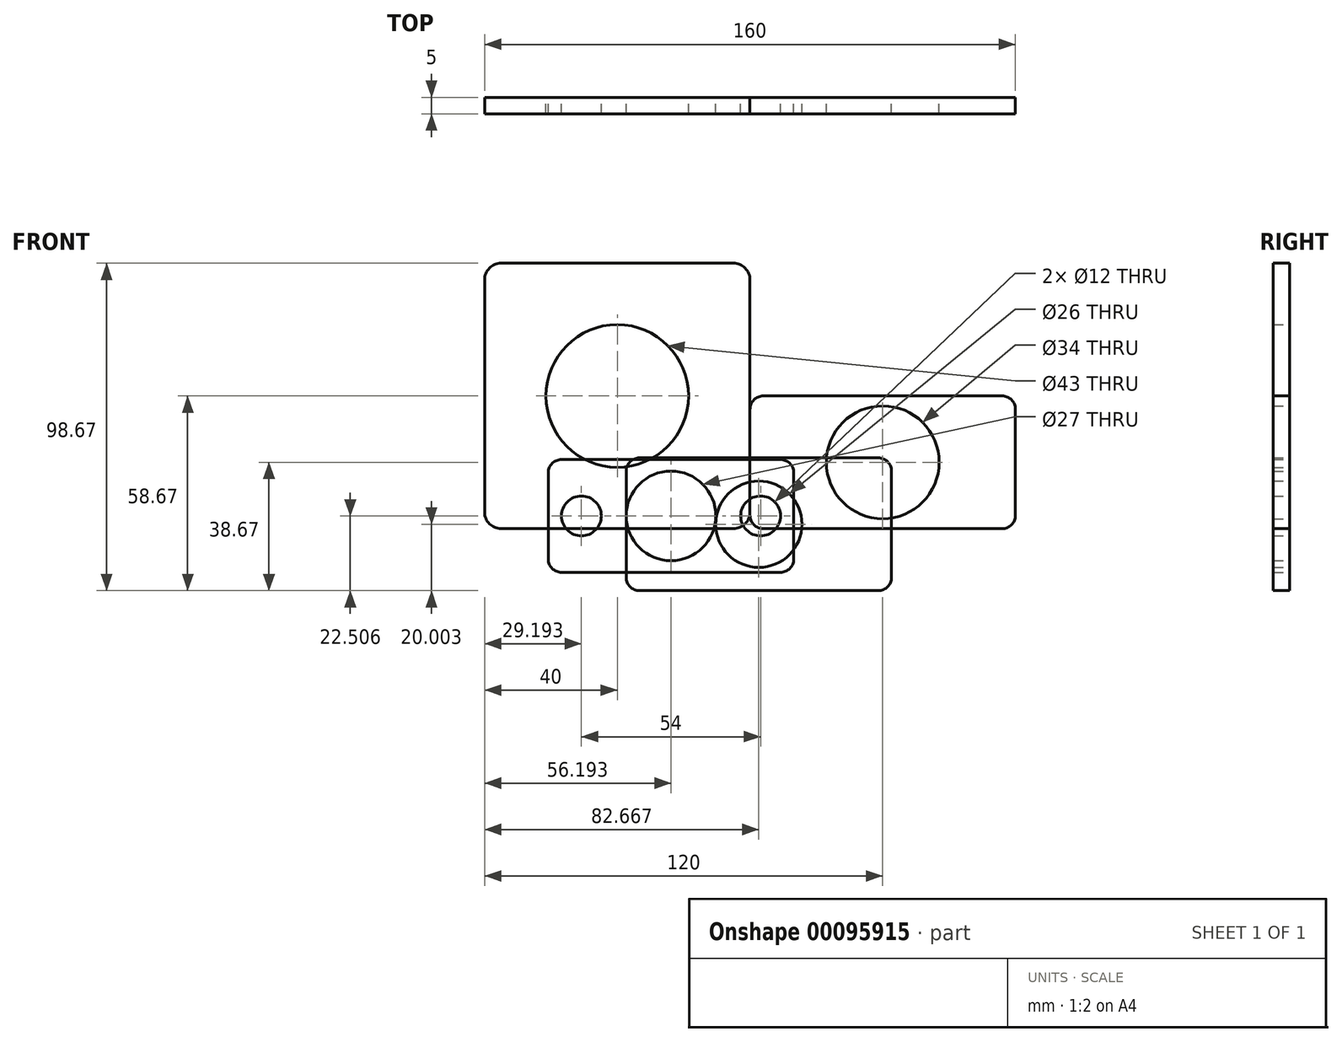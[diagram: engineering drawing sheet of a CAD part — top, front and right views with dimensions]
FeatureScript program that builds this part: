
annotation { "Feature Type Name" : "Feature", "Feature Type Description" : "" }
export const myFeature = defineFeature(function(context is Context, id is Id, definition is map)
    precondition{}
    {
        {
            var Q0;
            Q0=qCreatedBy(makeId("Front.planeOp"),FACE);
            var sketch = newSketch(context, id + "F0", { "sketchPlane" : qUnion([Q0])});
            skLineSegment(sketch, "E0.bottom", {"start": v(4, 0) * mm, "end": v(76, 0) * mm});
            skLineSegment(sketch, "E0.top", {"start": v(4, 40) * mm, "end": v(76, 40) * mm});
            skLineSegment(sketch, "E0.left", {"start": v(0, 4) * mm, "end": v(0, 36) * mm});
            skLineSegment(sketch, "E0.right", {"start": v(80, 4) * mm, "end": v(80, 36) * mm});
            skPoint(sketch, "E1.visualSharp", {"position": v(0, 40) * mm});
            skArc(sketch, "E1.filletArc", {"start": v(4, 40) * mm, "mid": v(1.17, 38.83) * mm, "end": v(0, 36) * mm});
            skPoint(sketch, "E2.visualSharp", {"position": v(80, 40) * mm});
            skArc(sketch, "E2.filletArc", {"start": v(80, 36) * mm, "mid": v(78.83, 38.83) * mm, "end": v(76, 40) * mm});
            skPoint(sketch, "E3.visualSharp", {"position": v(80, 0) * mm});
            skArc(sketch, "E3.filletArc", {"start": v(76, 0) * mm, "mid": v(78.83, 1.17) * mm, "end": v(80, 4) * mm});
            skPoint(sketch, "E4.visualSharp", {"position": v(0, 0) * mm});
            skArc(sketch, "E4.filletArc", {"start": v(0, 4) * mm, "mid": v(1.17, 1.17) * mm, "end": v(4, 0) * mm});
            skSolve(sketch);
        }
        {
            var Q0;
            Q0=makeQuery(id+"F0.imprint","IMPRINT",FACE,{"disambiguationData":[TD([[makeQuery(id+"F0.imprint","IMPRINT",EDGE,{"derivedFrom":sQuery(id+"F0.wireOp",EDGE,"E0.bottom")}),1.0]])]});
            extrude(context, id + "F1", {"entities" : qUnion([Q0]), "depth" : 5 * mm, "offsetDistance" : 25 * mm});
        }
        {
            var Q0;
            Q0=qCreatedBy(makeId("Front.planeOp"),FACE);
            var sketch = newSketch(context, id + "F2", { "sketchPlane" : qUnion([Q0])});
            skLineSegment(sketch, "E5.bottom", {"start": v(4, 0) * mm, "end": v(76, 0) * mm});
            skLineSegment(sketch, "E5.top", {"start": v(4, 40) * mm, "end": v(76, 40) * mm});
            skLineSegment(sketch, "E5.left", {"start": v(0, 4) * mm, "end": v(0, 36) * mm});
            skLineSegment(sketch, "E5.right", {"start": v(80, 4) * mm, "end": v(80, 36) * mm});
            skPoint(sketch, "E6.visualSharp", {"position": v(0, 40) * mm});
            skArc(sketch, "E6.filletArc", {"start": v(4, 40) * mm, "mid": v(1.17, 38.83) * mm, "end": v(0, 36) * mm});
            skPoint(sketch, "E7.visualSharp", {"position": v(80, 40) * mm});
            skArc(sketch, "E7.filletArc", {"start": v(80, 36) * mm, "mid": v(78.83, 38.83) * mm, "end": v(76, 40) * mm});
            skPoint(sketch, "E8.visualSharp", {"position": v(80, 0) * mm});
            skArc(sketch, "E8.filletArc", {"start": v(76, 0) * mm, "mid": v(78.83, 1.17) * mm, "end": v(80, 4) * mm});
            skPoint(sketch, "E9.visualSharp", {"position": v(0, 0) * mm});
            skArc(sketch, "E9.filletArc", {"start": v(0, 4) * mm, "mid": v(1.17, 1.17) * mm, "end": v(4, 0) * mm});
            skCircle(sketch, "E10", {"center": v(40, 20) * mm, "radius": 17 * mm});
            skPoint(sketch, "E10.centerSnap0", {"position": v(40, 0) * mm});
            skPoint(sketch, "E10.centerSnap1", {"position": v(0, 20) * mm});
            skSolve(sketch);
        }
        {
            var Q0;
            Q0=makeQuery(id+"F2.imprint","IMPRINT",FACE,{"disambiguationData":[TD([[makeQuery(id+"F2.imprint","IMPRINT",EDGE,{"derivedFrom":sQuery(id+"F2.wireOp",EDGE,"E5.bottom")}),1.0]])]});
            extrude(context, id + "F3", {"entities" : qUnion([Q0]), "depth" : 5 * mm, "offsetDistance" : 25 * mm});
        }
        {
            var Q0;
            Q0=qCreatedBy(makeId("Front.planeOp"),FACE);
            var sketch = newSketch(context, id + "F4", { "sketchPlane" : qUnion([Q0])});
            skLineSegment(sketch, "E11.bottom", {"start": v(-33.33, -18.67) * mm, "end": v(38.67, -18.67) * mm});
            skLineSegment(sketch, "E11.top", {"start": v(-33.33, 21.33) * mm, "end": v(38.67, 21.33) * mm});
            skLineSegment(sketch, "E11.left", {"start": v(-37.33, -14.67) * mm, "end": v(-37.33, 17.33) * mm});
            skLineSegment(sketch, "E11.right", {"start": v(42.67, -14.67) * mm, "end": v(42.67, 17.33) * mm});
            skPoint(sketch, "E12.visualSharp", {"position": v(-37.33, 21.33) * mm});
            skArc(sketch, "E12.filletArc", {"start": v(-33.33, 21.33) * mm, "mid": v(-36.16, 20.16) * mm, "end": v(-37.33, 17.33) * mm});
            skPoint(sketch, "E13.visualSharp", {"position": v(42.67, 21.33) * mm});
            skArc(sketch, "E13.filletArc", {"start": v(42.67, 17.33) * mm, "mid": v(41.5, 20.16) * mm, "end": v(38.67, 21.33) * mm});
            skPoint(sketch, "E14.visualSharp", {"position": v(42.67, -18.67) * mm});
            skArc(sketch, "E14.filletArc", {"start": v(38.67, -18.67) * mm, "mid": v(41.5, -17.5) * mm, "end": v(42.67, -14.67) * mm});
            skPoint(sketch, "E15.visualSharp", {"position": v(-37.33, -18.67) * mm});
            skArc(sketch, "E15.filletArc", {"start": v(-37.33, -14.67) * mm, "mid": v(-36.16, -17.5) * mm, "end": v(-33.33, -18.67) * mm});
            skCircle(sketch, "E16", {"center": v(2.67, 1.33) * mm, "radius": 13 * mm});
            skPoint(sketch, "E16.centerSnap0", {"position": v(2.67, -18.67) * mm});
            skPoint(sketch, "E16.centerSnap1", {"position": v(-37.33, 1.33) * mm});
            skSolve(sketch);
        }
        {
            var Q0;
            Q0 = qSketchRegion(id + "F4", true);
            extrude(context, id + "F5", {"entities" : qUnion([Q0]), "depth" : 5 * mm, "offsetDistance" : 25 * mm});
        }
        {
            var Q0;
            Q0=qCreatedBy(makeId("Front.planeOp"),FACE);
            var sketch = newSketch(context, id + "F6", { "sketchPlane" : qUnion([Q0])});
            skLineSegment(sketch, "E17.bottom", {"start": v(-56.8, -13.16) * mm, "end": v(9.2, -13.16) * mm});
            skLineSegment(sketch, "E17.top", {"start": v(-56.8, 20.84) * mm, "end": v(9.2, 20.84) * mm});
            skLineSegment(sketch, "E17.left", {"start": v(-60.8, -9.16) * mm, "end": v(-60.8, 16.84) * mm});
            skLineSegment(sketch, "E17.right", {"start": v(13.2, -9.16) * mm, "end": v(13.2, 16.84) * mm});
            skPoint(sketch, "E18.visualSharp", {"position": v(-60.8, 20.84) * mm});
            skArc(sketch, "E18.filletArc", {"start": v(-56.8, 20.84) * mm, "mid": v(-59.64, 19.66) * mm, "end": v(-60.8, 16.84) * mm});
            skPoint(sketch, "E19.visualSharp", {"position": v(13.2, 20.84) * mm});
            skArc(sketch, "E19.filletArc", {"start": v(13.2, 16.84) * mm, "mid": v(12.02, 19.66) * mm, "end": v(9.2, 20.84) * mm});
            skPoint(sketch, "E20.visualSharp", {"position": v(13.2, -13.16) * mm});
            skArc(sketch, "E20.filletArc", {"start": v(9.2, -13.16) * mm, "mid": v(12.02, -12) * mm, "end": v(13.2, -9.16) * mm});
            skPoint(sketch, "E21.visualSharp", {"position": v(-60.8, -13.16) * mm});
            skArc(sketch, "E21.filletArc", {"start": v(-60.8, -9.16) * mm, "mid": v(-59.64, -12) * mm, "end": v(-56.8, -13.16) * mm});
            skCircle(sketch, "E22", {"center": v(-23.8, 3.84) * mm, "radius": 13.5 * mm});
            skPoint(sketch, "E22.centerSnap0", {"position": v(-23.8, -13.16) * mm});
            skPoint(sketch, "E22.centerSnap1", {"position": v(-60.8, 3.84) * mm});
            skCircle(sketch, "E23", {"center": v(-50.8, 3.84) * mm, "radius": 6 * mm});
            skCircle(sketch, "E24", {"center": v(3.2, 3.84) * mm, "radius": 6 * mm});
            skPoint(sketch, "E24.centerSnap0", {"position": v(13.2, 3.84) * mm});
            skSolve(sketch);
        }
        {
            var Q0;
            Q0=makeQuery(id+"F6.imprint","IMPRINT",FACE,{"disambiguationData":[TD([[makeQuery(id+"F6.imprint","IMPRINT",EDGE,{"derivedFrom":sQuery(id+"F6.wireOp",EDGE,"E17.bottom")}),1.0]])]});
            extrude(context, id + "F7", {"entities" : qUnion([Q0]), "depth" : 5 * mm, "offsetDistance" : 25 * mm});
        }
        {
            var Q0;
            Q0=qCreatedBy(makeId("Front.planeOp"),FACE);
            var sketch = newSketch(context, id + "F8", { "sketchPlane" : qUnion([Q0])});
            skLineSegment(sketch, "E25.bottom", {"start": v(-5, 0) * mm, "end": v(-75, 0) * mm});
            skLineSegment(sketch, "E25.top", {"start": v(-5, 80) * mm, "end": v(-75, 80) * mm});
            skLineSegment(sketch, "E25.left", {"start": v(0, 5) * mm, "end": v(0, 75) * mm});
            skLineSegment(sketch, "E25.right", {"start": v(-80, 5) * mm, "end": v(-80, 75) * mm});
            skCircle(sketch, "E26", {"center": v(-40, 40) * mm, "radius": 21.5 * mm});
            skPoint(sketch, "E26.centerSnap0", {"position": v(-40, 0) * mm});
            skPoint(sketch, "E26.centerSnap1", {"position": v(0, 40) * mm});
            skPoint(sketch, "E27.visualSharp", {"position": v(-80, 80) * mm});
            skArc(sketch, "E27.filletArc", {"start": v(-75, 80) * mm, "mid": v(-78.54, 78.54) * mm, "end": v(-80, 75) * mm});
            skPoint(sketch, "E28.visualSharp", {"position": v(0, 80) * mm});
            skArc(sketch, "E28.filletArc", {"start": v(0, 75) * mm, "mid": v(-1.46, 78.54) * mm, "end": v(-5, 80) * mm});
            skPoint(sketch, "E29.visualSharp", {"position": v(0, 0) * mm});
            skArc(sketch, "E29.filletArc", {"start": v(-5, 0) * mm, "mid": v(-1.46, 1.46) * mm, "end": v(0, 5) * mm});
            skPoint(sketch, "E30.visualSharp", {"position": v(-80, 0) * mm});
            skArc(sketch, "E30.filletArc", {"start": v(-80, 5) * mm, "mid": v(-78.54, 1.46) * mm, "end": v(-75, 0) * mm});
            skSolve(sketch);
        }
        {
            var Q0;
            Q0 = qSketchRegion(id + "F8", true);
            extrude(context, id + "F9", {"entities" : qUnion([Q0]), "depth" : 5 * mm, "offsetDistance" : 25 * mm});
        }
    });
